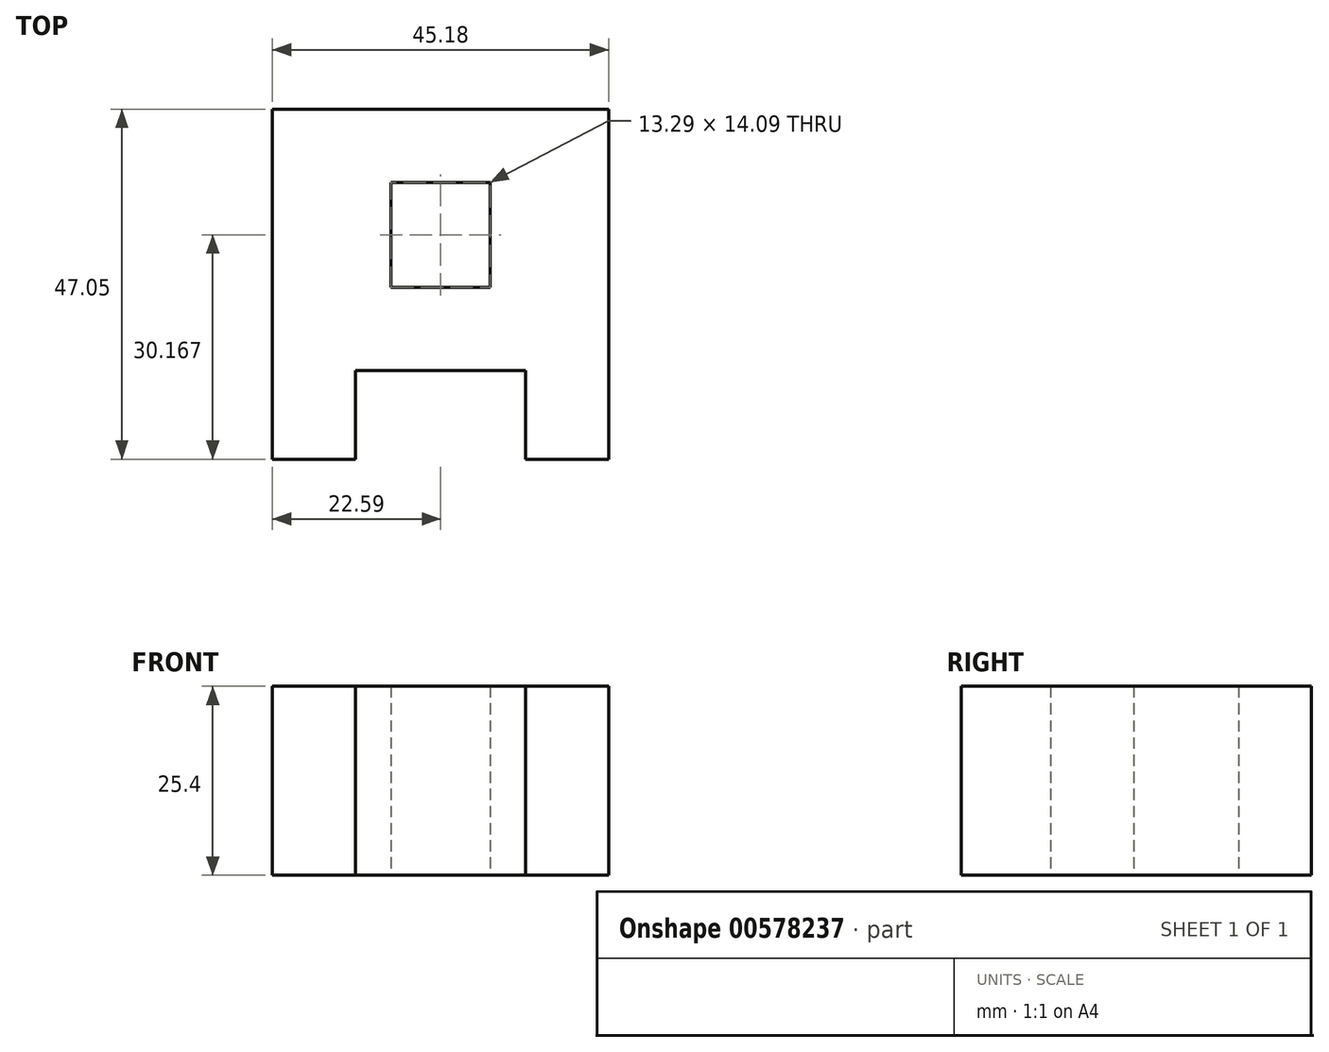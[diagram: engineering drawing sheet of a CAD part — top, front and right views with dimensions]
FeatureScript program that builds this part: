
annotation { "Feature Type Name" : "Feature", "Feature Type Description" : "" }
export const myFeature = defineFeature(function(context is Context, id is Id, definition is map)
    precondition{}
    {
        {
            var Q0;
            Q0=qCreatedBy(makeId("Top.planeOp"),FACE);
            var sketch = newSketch(context, id + "F0", { "sketchPlane" : qUnion([Q0])});
            skLineSegment(sketch, "E0", {"start": v(-22.6, 47.05) * mm, "end": v(0, 47.05) * mm});
            skLineSegment(sketch, "E1", {"start": v(0, 37.21) * mm, "end": v(-6.65, 37.21) * mm});
            skLineSegment(sketch, "E2", {"start": v(-6.65, 37.21) * mm, "end": v(-6.65, 23.12) * mm});
            skLineSegment(sketch, "E3", {"start": v(-6.65, 23.12) * mm, "end": v(0, 23.12) * mm});
            skLineSegment(sketch, "E4", {"start": v(0, 11.96) * mm, "end": v(-11.43, 11.96) * mm});
            skLineSegment(sketch, "E5", {"start": v(-11.43, 11.96) * mm, "end": v(-11.43, 0) * mm});
            skLineSegment(sketch, "E6", {"start": v(-22.6, 0) * mm, "end": v(-11.43, 0) * mm});
            skLineSegment(sketch, "E7", {"start": v(0, 23.12) * mm, "end": v(0, 11.96) * mm});
            skLineSegment(sketch, "E8.MirrorCS", {"start": v(22.6, 47.05) * mm, "end": v(22.6, 0) * mm});
            skLineSegment(sketch, "E9.MirrorCS", {"start": v(22.6, 47.05) * mm, "end": v(0, 47.05) * mm});
            skLineSegment(sketch, "E10.MirrorCS", {"start": v(0, 37.21) * mm, "end": v(6.65, 37.21) * mm});
            skLineSegment(sketch, "E11.MirrorCS", {"start": v(6.65, 37.21) * mm, "end": v(6.65, 23.12) * mm});
            skLineSegment(sketch, "E12.MirrorCS", {"start": v(6.65, 23.12) * mm, "end": v(0, 23.12) * mm});
            skLineSegment(sketch, "E13.MirrorCS", {"start": v(0, 11.96) * mm, "end": v(11.43, 11.96) * mm});
            skLineSegment(sketch, "E14.MirrorCS", {"start": v(22.6, 0) * mm, "end": v(11.43, 0) * mm});
            skLineSegment(sketch, "E15.MirrorCS", {"start": v(11.43, 11.96) * mm, "end": v(11.43, 0) * mm});
            skLineSegment(sketch, "E16", {"start": v(-22.6, 47.05) * mm, "end": v(-22.6, 0) * mm});
            skSolve(sketch);
        }
        {
            var Q0;
            Q0 = qSketchRegion(id + "F0", true);
            extrude(context, id + "F1", {"entities" : qUnion([Q0]), "depth" : 25.4 * mm, "offsetDistance" : 25.4 * mm});
        }
    });
